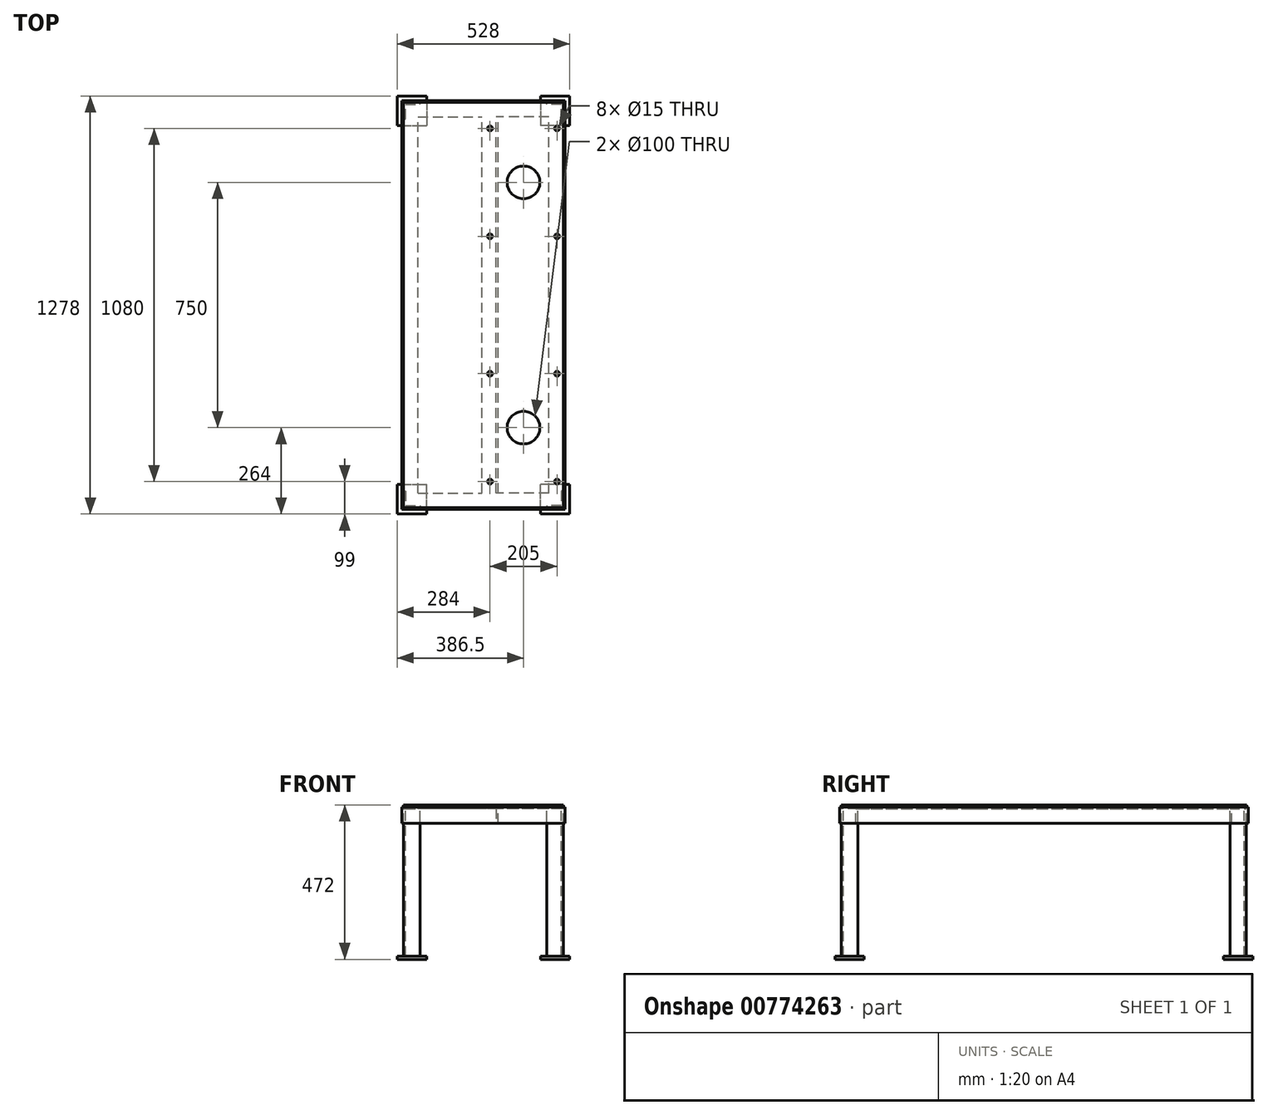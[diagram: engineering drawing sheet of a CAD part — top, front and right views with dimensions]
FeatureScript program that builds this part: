
annotation { "Feature Type Name" : "Feature", "Feature Type Description" : "" }
export const myFeature = defineFeature(function(context is Context, id is Id, definition is map)
    precondition{}
    {
        {
            var Q0;
            Q0=qCreatedBy(makeId("Right.planeOp"),FACE);
            var sketch = newSketch(context, id + "F0", { "sketchPlane" : qUnion([Q0])});
            skLineSegment(sketch, "E0", {"start": v(-625, 0) * mm, "end": v(-575, 0) * mm});
            skLineSegment(sketch, "E1", {"start": v(-575, 0) * mm, "end": v(-575, -6) * mm});
            skLineSegment(sketch, "E2", {"start": v(-575, -6) * mm, "end": v(-619, -6) * mm});
            skLineSegment(sketch, "E3", {"start": v(-619, -6) * mm, "end": v(-619, -50) * mm});
            skLineSegment(sketch, "E4", {"start": v(-619, -50) * mm, "end": v(-625, -50) * mm});
            skLineSegment(sketch, "E5", {"start": v(-625, -50) * mm, "end": v(-625, 0) * mm});
            skLineSegment(sketch, "E6.MirrorCS", {"start": v(575, 0) * mm, "end": v(575, -6) * mm});
            skLineSegment(sketch, "E7.MirrorCS", {"start": v(619, -50) * mm, "end": v(625, -50) * mm});
            skLineSegment(sketch, "E8.MirrorCS", {"start": v(619, -6) * mm, "end": v(619, -50) * mm});
            skLineSegment(sketch, "E9.MirrorCS", {"start": v(625, 0) * mm, "end": v(575, 0) * mm});
            skLineSegment(sketch, "E10.MirrorCS", {"start": v(575, -6) * mm, "end": v(619, -6) * mm});
            skLineSegment(sketch, "E11.MirrorCS", {"start": v(625, -50) * mm, "end": v(625, 0) * mm});
            skSolve(sketch);
        }
        {
            var Q0;
            Q0 = qSketchRegion(id + "F0", true);
            extrude(context, id + "F1", {"entities" : qUnion([Q0]), "endBound" : BoundingType.SYMMETRIC, "depth" : 500 * mm, "offsetDistance" : 25 * mm});
        }
        {
            var Q0;
            Q0=qCreatedBy(makeId("Front.planeOp"),FACE);
            var sketch = newSketch(context, id + "F2", { "sketchPlane" : qUnion([Q0])});
            skLineSegment(sketch, "E12", {"start": v(-200, 0) * mm, "end": v(-250, 0) * mm});
            skLineSegment(sketch, "E13", {"start": v(-250, 0) * mm, "end": v(-250, -50) * mm});
            skLineSegment(sketch, "E14", {"start": v(-250, -50) * mm, "end": v(-244, -50) * mm});
            skLineSegment(sketch, "E15", {"start": v(-244, -50) * mm, "end": v(-244, -6) * mm});
            skLineSegment(sketch, "E16", {"start": v(-244, -6) * mm, "end": v(-200, -6) * mm});
            skLineSegment(sketch, "E17", {"start": v(-200, -6) * mm, "end": v(-200, 0) * mm});
            skLineSegment(sketch, "E18.MirrorCS", {"start": v(200, -6) * mm, "end": v(200, 0) * mm});
            skLineSegment(sketch, "E19.MirrorCS", {"start": v(250, -50) * mm, "end": v(244, -50) * mm});
            skLineSegment(sketch, "E20.MirrorCS", {"start": v(244, -50) * mm, "end": v(244, -6) * mm});
            skLineSegment(sketch, "E21.MirrorCS", {"start": v(200, 0) * mm, "end": v(250, 0) * mm});
            skLineSegment(sketch, "E22.MirrorCS", {"start": v(250, 0) * mm, "end": v(250, -50) * mm});
            skLineSegment(sketch, "E23.MirrorCS", {"start": v(244, -6) * mm, "end": v(200, -6) * mm});
            skSolve(sketch);
        }
        {
            var Q0;
            Q0 = qSketchRegion(id + "F2", true);
            extrude(context, id + "F3", {"entities" : qUnion([Q0]), "operationType" : NewBodyOperationType.ADD, "endBound" : BoundingType.SYMMETRIC, "depth" : 1250 * mm, "offsetDistance" : 25 * mm});
        }
        {
            var Q0;
            Q0=makeQuery(id+"F3.boolean.opBoolean","MERGE",FACE,{"derivedFrom":[makeQuery(id+"F1.opExtrude","SWEPT_FACE",FACE,{"disambiguationData":[OSD([sQuery(id+"F0.wireOp",EDGE,"E2")])]}),makeQuery(id+"F1.opExtrude","SWEPT_FACE",FACE,{"disambiguationData":[OSD([sQuery(id+"F0.wireOp",EDGE,"E10.MirrorCS")])]}),makeQuery(id+"F3.opExtrude","SWEPT_FACE",FACE,{"disambiguationData":[OSD([sQuery(id+"F2.wireOp",EDGE,"E16")])]}),makeQuery(id+"F3.opExtrude","SWEPT_FACE",FACE,{"disambiguationData":[OSD([sQuery(id+"F2.wireOp",EDGE,"E23.MirrorCS")])]})]});
            var sketch = newSketch(context, id + "F4", { "sketchPlane" : qUnion([Q0])});
            skLineSegment(sketch, "E24", {"start": v(244, 619) * mm, "end": v(244, 569) * mm});
            skLineSegment(sketch, "E25", {"start": v(244, 569) * mm, "end": v(238, 569) * mm});
            skLineSegment(sketch, "E26", {"start": v(238, 569) * mm, "end": v(238, 613) * mm});
            skLineSegment(sketch, "E27", {"start": v(238, 613) * mm, "end": v(194, 613) * mm});
            skLineSegment(sketch, "E28", {"start": v(194, 613) * mm, "end": v(194, 619) * mm});
            skLineSegment(sketch, "E29", {"start": v(194, 619) * mm, "end": v(244, 619) * mm});
            skLineSegment(sketch, "E30.MirrorCS", {"start": v(244, -569) * mm, "end": v(238, -569) * mm});
            skLineSegment(sketch, "E31.MirrorCS", {"start": v(194, -613) * mm, "end": v(194, -619) * mm});
            skLineSegment(sketch, "E32.MirrorCS", {"start": v(244, -619) * mm, "end": v(244, -569) * mm});
            skLineSegment(sketch, "E33.MirrorCS", {"start": v(238, -613) * mm, "end": v(194, -613) * mm});
            skLineSegment(sketch, "E34.MirrorCS", {"start": v(238, -569) * mm, "end": v(238, -613) * mm});
            skLineSegment(sketch, "E35.MirrorCS", {"start": v(194, -619) * mm, "end": v(244, -619) * mm});
            skLineSegment(sketch, "E36.MirrorCS", {"start": v(-194, -613) * mm, "end": v(-194, -619) * mm});
            skLineSegment(sketch, "E37.MirrorCS", {"start": v(-244, -569) * mm, "end": v(-238, -569) * mm});
            skLineSegment(sketch, "E38.MirrorCS", {"start": v(-194, 613) * mm, "end": v(-194, 619) * mm});
            skLineSegment(sketch, "E39.MirrorCS", {"start": v(-244, 569) * mm, "end": v(-238, 569) * mm});
            skLineSegment(sketch, "E40.MirrorCS", {"start": v(-238, 613) * mm, "end": v(-194, 613) * mm});
            skLineSegment(sketch, "E41.MirrorCS", {"start": v(-238, 569) * mm, "end": v(-238, 613) * mm});
            skLineSegment(sketch, "E42.MirrorCS", {"start": v(-244, 619) * mm, "end": v(-244, 569) * mm});
            skLineSegment(sketch, "E43.MirrorCS", {"start": v(-194, 619) * mm, "end": v(-244, 619) * mm});
            skLineSegment(sketch, "E44.MirrorCS", {"start": v(-194, -619) * mm, "end": v(-244, -619) * mm});
            skLineSegment(sketch, "E45.MirrorCS", {"start": v(-238, -569) * mm, "end": v(-238, -613) * mm});
            skLineSegment(sketch, "E46.MirrorCS", {"start": v(-238, -613) * mm, "end": v(-194, -613) * mm});
            skLineSegment(sketch, "E47.MirrorCS", {"start": v(-244, -619) * mm, "end": v(-244, -569) * mm});
            skSolve(sketch);
        }
        {
            var Q0;
            Q0 = qSketchRegion(id + "F4", true);
            extrude(context, id + "F5", {"entities" : qUnion([Q0]), "operationType" : NewBodyOperationType.ADD, "depth" : 450 * mm, "offsetDistance" : 25 * mm});
        }
        {
            var Q0;
            Q0=makeQuery(id+"F5.opExtrude","CAP_FACE",FACE,{"disambiguationData":[OSD([sQuery(id+"F4.wireOp",EDGE,"E36.MirrorCS"),sQuery(id+"F4.wireOp",EDGE,"E37.MirrorCS"),sQuery(id+"F4.wireOp",EDGE,"E44.MirrorCS"),sQuery(id+"F4.wireOp",EDGE,"E45.MirrorCS"),sQuery(id+"F4.wireOp",EDGE,"E46.MirrorCS"),sQuery(id+"F4.wireOp",EDGE,"E47.MirrorCS")])],"isStart":false});
            var sketch = newSketch(context, id + "F6", { "sketchPlane" : qUnion([Q0])});
            skLineSegment(sketch, "E48.bottom", {"start": v(-264, -639) * mm, "end": v(-174, -639) * mm});
            skLineSegment(sketch, "E48.top", {"start": v(-264, -549) * mm, "end": v(-174, -549) * mm});
            skLineSegment(sketch, "E48.left", {"start": v(-264, -639) * mm, "end": v(-264, -549) * mm});
            skLineSegment(sketch, "E48.right", {"start": v(-174, -639) * mm, "end": v(-174, -549) * mm});
            skLineSegment(sketch, "E49.MirrorCS", {"start": v(-264, 639) * mm, "end": v(-174, 639) * mm});
            skLineSegment(sketch, "E50.MirrorCS", {"start": v(-174, 639) * mm, "end": v(-174, 549) * mm});
            skLineSegment(sketch, "E51.MirrorCS", {"start": v(-264, 639) * mm, "end": v(-264, 549) * mm});
            skLineSegment(sketch, "E52.MirrorCS", {"start": v(-264, 549) * mm, "end": v(-174, 549) * mm});
            skLineSegment(sketch, "E53.MirrorCS", {"start": v(264, 549) * mm, "end": v(174, 549) * mm});
            skLineSegment(sketch, "E54.MirrorCS", {"start": v(264, 639) * mm, "end": v(264, 549) * mm});
            skLineSegment(sketch, "E55.MirrorCS", {"start": v(174, 639) * mm, "end": v(174, 549) * mm});
            skLineSegment(sketch, "E56.MirrorCS", {"start": v(264, 639) * mm, "end": v(174, 639) * mm});
            skLineSegment(sketch, "E57.MirrorCS", {"start": v(174, -639) * mm, "end": v(174, -549) * mm});
            skLineSegment(sketch, "E58.MirrorCS", {"start": v(264, -639) * mm, "end": v(264, -549) * mm});
            skLineSegment(sketch, "E59.MirrorCS", {"start": v(264, -639) * mm, "end": v(174, -639) * mm});
            skLineSegment(sketch, "E60.MirrorCS", {"start": v(264, -549) * mm, "end": v(174, -549) * mm});
            skSolve(sketch);
        }
        {
            var Q0;
            Q0 = qSketchRegion(id + "F6", true);
            extrude(context, id + "F7", {"entities" : qUnion([Q0]), "operationType" : NewBodyOperationType.ADD, "depth" : 10 * mm, "offsetDistance" : 25 * mm});
        }
        {
            var Q0;
            Q0=makeQuery(id+"F3.boolean.opBoolean","MERGE",FACE,{"derivedFrom":[makeQuery(id+"F1.opExtrude","SWEPT_FACE",FACE,{"disambiguationData":[OSD([sQuery(id+"F0.wireOp",EDGE,"E0")])]}),makeQuery(id+"F1.opExtrude","SWEPT_FACE",FACE,{"disambiguationData":[OSD([sQuery(id+"F0.wireOp",EDGE,"E9.MirrorCS")])]}),makeQuery(id+"F3.opExtrude","SWEPT_FACE",FACE,{"disambiguationData":[OSD([sQuery(id+"F2.wireOp",EDGE,"E12")])]}),makeQuery(id+"F3.opExtrude","SWEPT_FACE",FACE,{"disambiguationData":[OSD([sQuery(id+"F2.wireOp",EDGE,"E21.MirrorCS")])]})]});
            var sketch = newSketch(context, id + "F8", { "sketchPlane" : qUnion([Q0])});
            skLineSegment(sketch, "E61.bottom", {"start": v(-245, 620) * mm, "end": v(245, 620) * mm});
            skLineSegment(sketch, "E61.top", {"start": v(-245, -620) * mm, "end": v(245, -620) * mm});
            skLineSegment(sketch, "E61.left", {"start": v(-245, 620) * mm, "end": v(-245, -620) * mm});
            skLineSegment(sketch, "E61.right", {"start": v(245, 620) * mm, "end": v(245, -620) * mm});
            skPoint(sketch, "E61.middle", {"position": v(0, 0) * mm});
            skSolve(sketch);
        }
        {
            var Q0;
            Q0 = qSketchRegion(id + "F8", true);
            extrude(context, id + "F9", {"entities" : qUnion([Q0]), "depth" : 6 * mm, "offsetDistance" : 25 * mm});
        }
        {
            var Q0;
            Q0=qCreatedBy(makeId("Front.planeOp"),FACE);
            var sketch = newSketch(context, id + "F10", { "sketchPlane" : qUnion([Q0])});
            skLineSegment(sketch, "E62", {"start": v(45, 0) * mm, "end": v(-5, 0) * mm});
            skLineSegment(sketch, "E63", {"start": v(-5, 0) * mm, "end": v(-5, -6) * mm});
            skLineSegment(sketch, "E64", {"start": v(-5, -6) * mm, "end": v(39, -6) * mm});
            skLineSegment(sketch, "E65", {"start": v(39, -6) * mm, "end": v(39, -50) * mm});
            skLineSegment(sketch, "E66", {"start": v(39, -50) * mm, "end": v(45, -50) * mm});
            skLineSegment(sketch, "E67", {"start": v(45, -50) * mm, "end": v(45, 0) * mm});
            skSolve(sketch);
        }
        {
            var Q0;
            Q0 = qSketchRegion(id + "F10", true);
            extrude(context, id + "F11", {"entities" : qUnion([Q0]), "operationType" : NewBodyOperationType.ADD, "endBound" : BoundingType.SYMMETRIC, "depth" : 1150 * mm, "offsetDistance" : 25 * mm});
        }
        {
            var Q0;
            Q0=makeQuery(id+"F9.opExtrude","CAP_FACE",FACE,{"disambiguationData":[OSD([sQuery(id+"F8.wireOp",EDGE,"E61.bottom"),sQuery(id+"F8.wireOp",EDGE,"E61.top"),sQuery(id+"F8.wireOp",EDGE,"E61.left"),sQuery(id+"F8.wireOp",EDGE,"E61.right")])],"isStart":false});
            var sketch = newSketch(context, id + "F12", { "sketchPlane" : qUnion([Q0])});
            skLineSegment(sketch, "E68", {"start": v(225, -210) * mm, "end": v(20, -210) * mm, "construction": true});
            skLineSegment(sketch, "E69", {"start": v(20, -210) * mm, "end": v(20, -540) * mm, "construction": true});
            skLineSegment(sketch, "E70", {"start": v(20, -540) * mm, "end": v(225, -540) * mm, "construction": true});
            skLineSegment(sketch, "E71", {"start": v(225, -540) * mm, "end": v(225, -210) * mm, "construction": true});
            skCircle(sketch, "E72", {"center": v(20, -210) * mm, "radius": 7.5 * mm});
            skCircle(sketch, "E73", {"center": v(225, -210) * mm, "radius": 7.5 * mm});
            skCircle(sketch, "E74", {"center": v(225, -540) * mm, "radius": 7.5 * mm});
            skCircle(sketch, "E75", {"center": v(20, -540) * mm, "radius": 7.5 * mm});
            skCircle(sketch, "E76.MirrorC", {"center": v(20, 540) * mm, "radius": 7.5 * mm});
            skCircle(sketch, "E77.MirrorC", {"center": v(225, 540) * mm, "radius": 7.5 * mm});
            skCircle(sketch, "E78.MirrorC", {"center": v(225, 210) * mm, "radius": 7.5 * mm});
            skCircle(sketch, "E79.MirrorC", {"center": v(20, 210) * mm, "radius": 7.5 * mm});
            skLineSegment(sketch, "E80.MirrorCS", {"start": v(225, 540) * mm, "end": v(225, 210) * mm, "construction": true});
            skLineSegment(sketch, "E81.MirrorCS", {"start": v(20, 540) * mm, "end": v(225, 540) * mm, "construction": true});
            skLineSegment(sketch, "E82.MirrorCS", {"start": v(20, 210) * mm, "end": v(20, 540) * mm, "construction": true});
            skLineSegment(sketch, "E83.MirrorCS", {"start": v(225, 210) * mm, "end": v(20, 210) * mm, "construction": true});
            skCircle(sketch, "E84", {"center": v(122.5, -375) * mm, "radius": 50 * mm});
            skPoint(sketch, "E84.centerSnap0", {"position": v(122.5, -210) * mm});
            skPoint(sketch, "E84.centerSnap1", {"position": v(20, -375) * mm});
            skCircle(sketch, "E85.MirrorC", {"center": v(122.5, 375) * mm, "radius": 50 * mm});
            skSolve(sketch);
        }
        {
            var Q0;
            Q0 = qSketchRegion(id + "F12", true);
            extrude(context, id + "F13", {"entities" : qUnion([Q0]), "operationType" : NewBodyOperationType.REMOVE, "oppositeDirection" : true, "depth" : 12 * mm, "offsetDistance" : 25 * mm});
        }
    });
